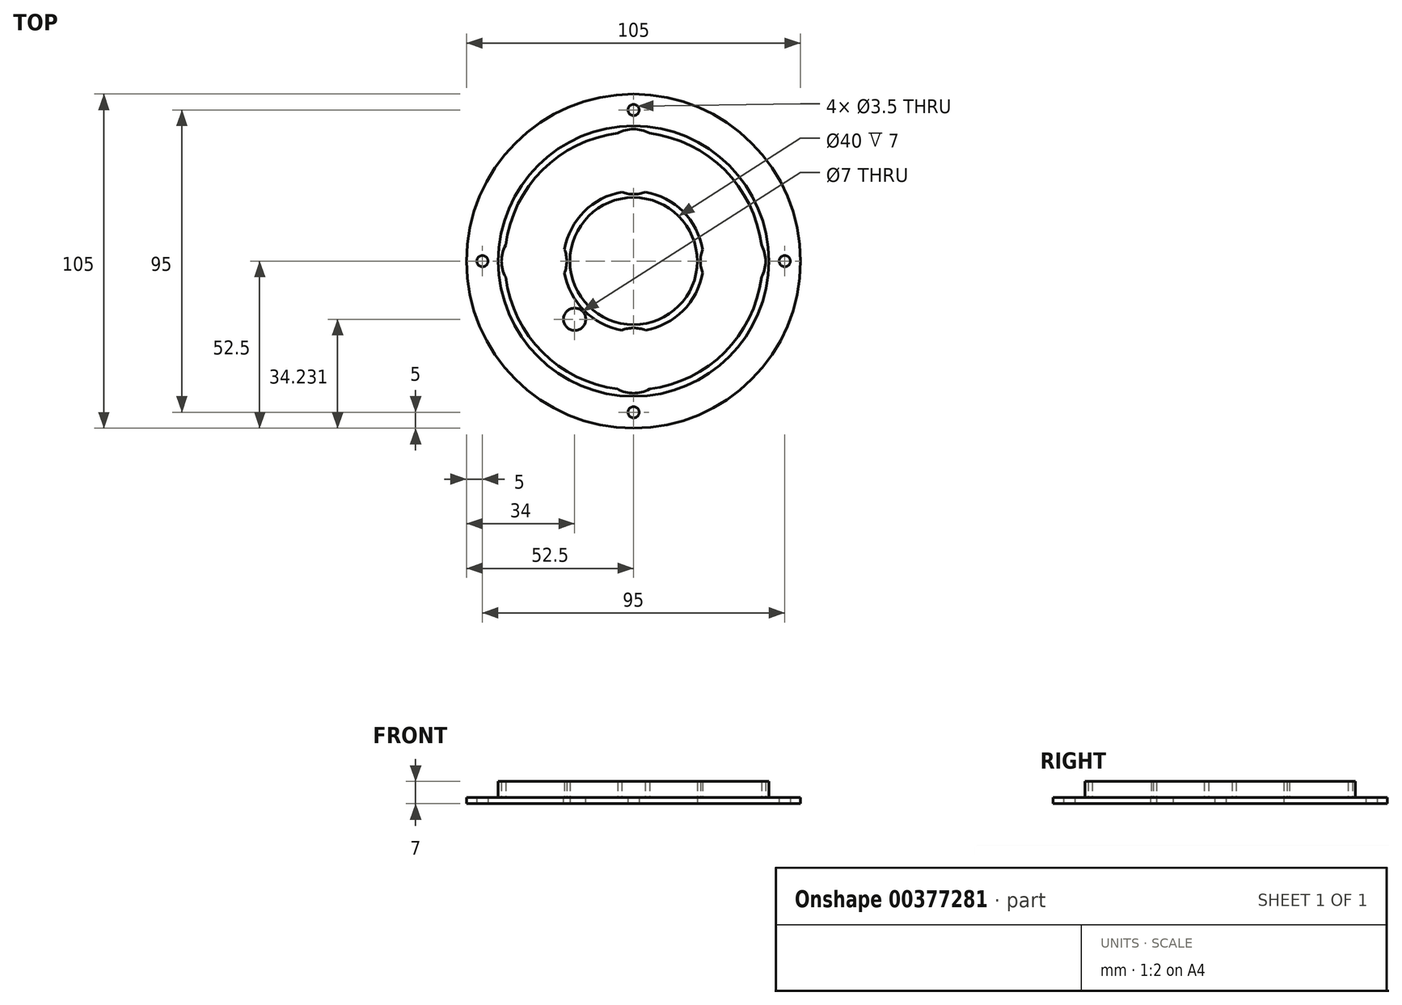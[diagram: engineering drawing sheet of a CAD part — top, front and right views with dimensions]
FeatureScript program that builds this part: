
annotation { "Feature Type Name" : "Feature", "Feature Type Description" : "" }
export const myFeature = defineFeature(function(context is Context, id is Id, definition is map)
    precondition{}
    {
        {
            var Q0;
            Q0=qCreatedBy(makeId("Top.planeOp"),FACE);
            var sketch = newSketch(context, id + "F0", { "sketchPlane" : qUnion([Q0])});
            skCircle(sketch, "E0", {"center": v(0, 0) * mm, "radius": 52.5 * mm});
            skCircle(sketch, "E1", {"center": v(0, 0) * mm, "radius": 42.5 * mm});
            skCircle(sketch, "E2", {"center": v(0, 0) * mm, "radius": 20 * mm});
            skLineSegment(sketch, "E3", {"start": v(0, 52.5) * mm, "end": v(0, 47.5) * mm, "construction": true});
            skLineSegment(sketch, "E4", {"start": v(52.5, 0) * mm, "end": v(47.5, 0) * mm, "construction": true});
            skLineSegment(sketch, "E5", {"start": v(0, -52.5) * mm, "end": v(0, -47.5) * mm, "construction": true});
            skLineSegment(sketch, "E6", {"start": v(-52.5, 0) * mm, "end": v(-47.5, 0) * mm, "construction": true});
            skCircle(sketch, "E7", {"center": v(0, 47.5) * mm, "radius": 1.75 * mm});
            skCircle(sketch, "E8", {"center": v(-47.5, 0) * mm, "radius": 1.75 * mm});
            skCircle(sketch, "E9", {"center": v(0, -47.5) * mm, "radius": 1.75 * mm});
            skCircle(sketch, "E10", {"center": v(47.5, 0) * mm, "radius": 1.75 * mm});
            skLineSegment(sketch, "E11", {"start": v(-42.5, 0) * mm, "end": v(-20, 0) * mm, "construction": true});
            skLineSegment(sketch, "E12", {"start": v(0, 42.5) * mm, "end": v(0, 20) * mm, "construction": true});
            skLineSegment(sketch, "E13", {"start": v(42.5, 0) * mm, "end": v(20, 0) * mm, "construction": true});
            skLineSegment(sketch, "E14", {"start": v(0, -42.5) * mm, "end": v(0, -20) * mm, "construction": true});
            skSolve(sketch);
        }
        {
            var Q0;
            Q0=makeQuery(id+"F0.imprint","IMPRINT",FACE,{"disambiguationData":[TD([[makeQuery(id+"F0.imprint","IMPRINT",EDGE,{"derivedFrom":sQuery(id+"F0.wireOp",EDGE,"E0")}),1.0]])]});
            extrude(context, id + "F1", {"entities" : qUnion([Q0]), "depth" : 2 * mm});
        }
        {
            var Q0;
            Q0=makeQuery(id+"F0.imprint","IMPRINT",FACE,{"disambiguationData":[TD([[makeQuery(id+"F0.imprint","IMPRINT",EDGE,{"derivedFrom":sQuery(id+"F0.wireOp",EDGE,"E1")}),1.0]])]});
            extrude(context, id + "F2", {"entities" : qUnion([Q0]), "operationType" : NewBodyOperationType.ADD, "depth" : 7 * mm});
        }
        {
            var Q0;
            Q0=makeQuery(id+"F2.opExtrude","CAP_FACE",FACE,{"disambiguationData":[OSD([sQuery(id+"F0.wireOp",EDGE,"E1"),sQuery(id+"F0.wireOp",EDGE,"E2")])],"isStart":false});
            shell(context, id + "F3", {"entities" : qUnion([Q0]), "thickness" : 2 * mm});
        }
        {
            var Q0;
            Q0=makeQuery(id+"F3.opShell","OFFSET_FACE",FACE,{"disambiguationData":[OSD([sQuery(id+"F0.wireOp",EDGE,"E0"),sQuery(id+"F0.wireOp",EDGE,"E1"),sQuery(id+"F0.wireOp",EDGE,"E2"),sQuery(id+"F0.wireOp",EDGE,"E7"),sQuery(id+"F0.wireOp",EDGE,"E8"),sQuery(id+"F0.wireOp",EDGE,"E9"),sQuery(id+"F0.wireOp",EDGE,"E10")])]});
            var sketch = newSketch(context, id + "F4", { "sketchPlane" : qUnion([Q0])});
            skLineSegment(sketch, "E15", {"start": v(0, 0) * mm, "end": v(-31.25, 0) * mm, "construction": true});
            skLineSegment(sketch, "E16", {"start": v(0, 0) * mm, "end": v(0, 31.25) * mm, "construction": true});
            skLineSegment(sketch, "E17", {"start": v(0, 0) * mm, "end": v(31.25, 0) * mm, "construction": true});
            skLineSegment(sketch, "E18", {"start": v(0, 0) * mm, "end": v(0, -31.25) * mm, "construction": true});
            skCircle(sketch, "E19", {"center": v(0, 31.25) * mm, "radius": 10.25 * mm});
            skCircle(sketch, "E20", {"center": v(-31.25, 0) * mm, "radius": 10.25 * mm});
            skCircle(sketch, "E21", {"center": v(0, -31.25) * mm, "radius": 10.25 * mm});
            skCircle(sketch, "E22", {"center": v(31.25, 0) * mm, "radius": 10.25 * mm});
            skSolve(sketch);
        }
        {
            var Q0;
            Q0 = qSketchRegion(id + "F4", true);
            extrude(context, id + "F5", {"entities" : qUnion([Q0]), "operationType" : NewBodyOperationType.REMOVE, "depth" : 25 * mm});
        }
        {
            var Q0;
            Q0=makeQuery(id+"F5.boolean.opBoolean","MERGE",FACE,{"derivedFrom":[makeQuery(id+"F3.opShell","OFFSET_FACE",FACE,{"disambiguationData":[OSD([sQuery(id+"F0.wireOp",EDGE,"E0"),sQuery(id+"F0.wireOp",EDGE,"E1"),sQuery(id+"F0.wireOp",EDGE,"E2"),sQuery(id+"F0.wireOp",EDGE,"E7"),sQuery(id+"F0.wireOp",EDGE,"E8"),sQuery(id+"F0.wireOp",EDGE,"E9"),sQuery(id+"F0.wireOp",EDGE,"E10")])]}),makeQuery(id+"F5.opExtrude","CAP_FACE",FACE,{"disambiguationData":[OSD([sQuery(id+"F4.wireOp",EDGE,"E19")])],"isStart":true}),makeQuery(id+"F5.opExtrude","CAP_FACE",FACE,{"disambiguationData":[OSD([sQuery(id+"F4.wireOp",EDGE,"E20")])],"isStart":true}),makeQuery(id+"F5.opExtrude","CAP_FACE",FACE,{"disambiguationData":[OSD([sQuery(id+"F4.wireOp",EDGE,"E21")])],"isStart":true}),makeQuery(id+"F5.opExtrude","CAP_FACE",FACE,{"disambiguationData":[OSD([sQuery(id+"F4.wireOp",EDGE,"E22")])],"isStart":true})]});
            var sketch = newSketch(context, id + "F6", { "sketchPlane" : qUnion([Q0])});
            skLineSegment(sketch, "E23", {"start": v(0, 0) * mm, "end": v(-18.5, -18.27) * mm, "construction": true});
            skCircle(sketch, "E24", {"center": v(-18.5, -18.27) * mm, "radius": 3.5 * mm});
            skSolve(sketch);
        }
        {
            var Q0;
            Q0 = qSketchRegion(id + "F6", true);
            extrude(context, id + "F7", {"entities" : qUnion([Q0]), "operationType" : NewBodyOperationType.REMOVE, "oppositeDirection" : true, "depth" : 25 * mm});
        }
    });
